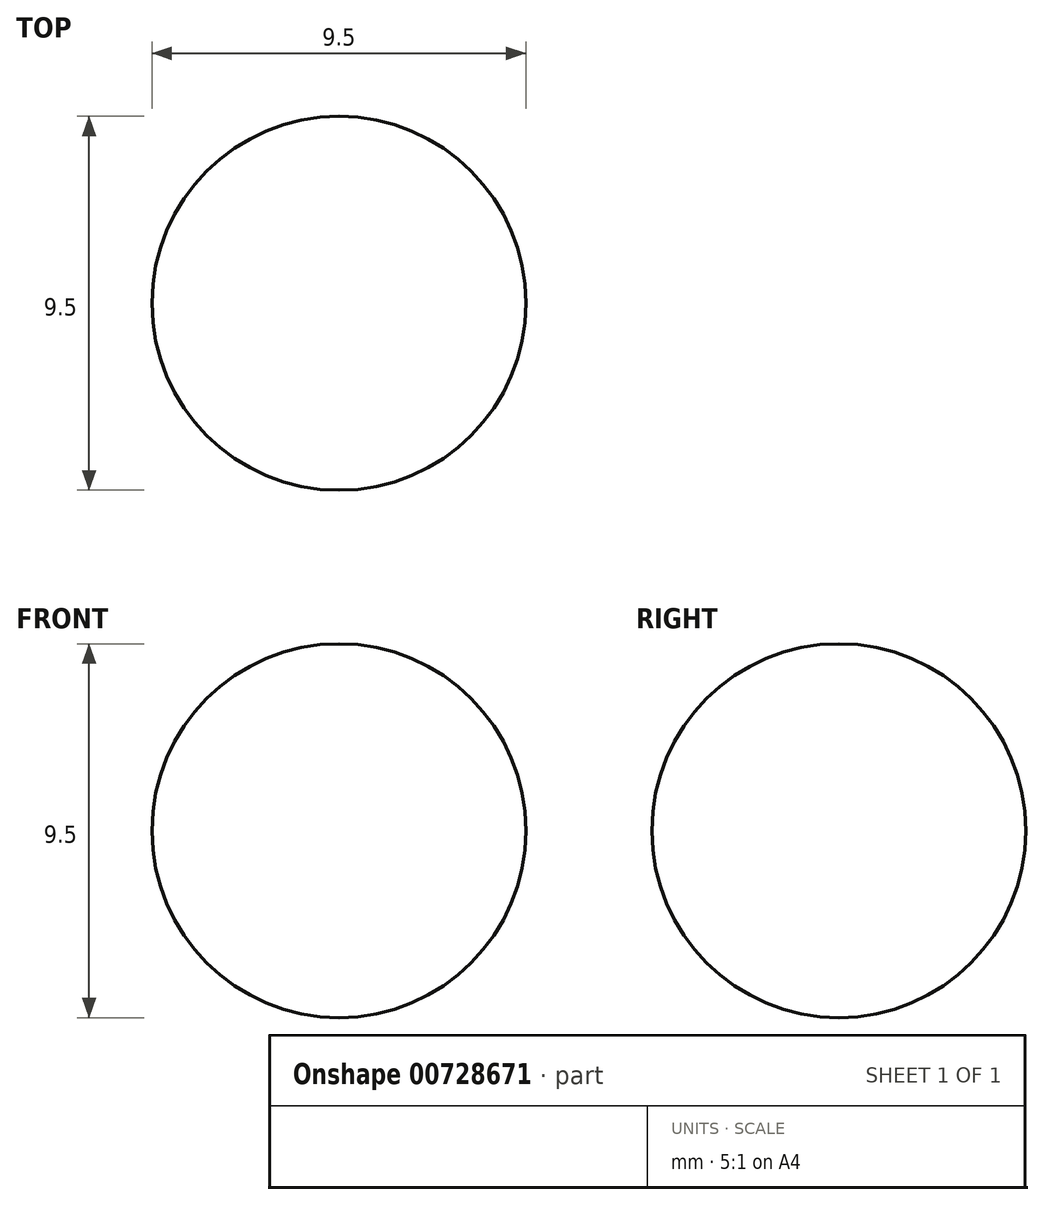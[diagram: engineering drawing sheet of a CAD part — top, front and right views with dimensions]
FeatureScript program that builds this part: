
annotation { "Feature Type Name" : "Feature", "Feature Type Description" : "" }
export const myFeature = defineFeature(function(context is Context, id is Id, definition is map)
    precondition{}
    {
        {
            var Q0;
            Q0=qCreatedBy(makeId("Front.planeOp"),FACE);
            var sketch = newSketch(context, id + "F0", { "sketchPlane" : qUnion([Q0])});
            skCircle(sketch, "E0", {"center": v(0, 0) * mm, "radius": 4.75 * mm});
            skLineSegment(sketch, "E1", {"start": v(-4.75, 0) * mm, "end": v(4.75, 0) * mm});
            skSolve(sketch);
        }
        {
            var Q0;
            {var subQ0=sQuery(id+"F0.wireOp",EDGE,"E1");Q0=makeQuery(id+"F0.imprint","IMPRINT",FACE,{"disambiguationData":[TD([[makeQuery(id+"F0.imprint","IMPRINT",EDGE,{"derivedFrom":subQ0}),1.0]])]});}
            var Q1;
            Q1=sQuery(id+"F0.wireOp",EDGE,"E1");
            revolve(context, id + "F1", {"surfaceOperationType" : NewSurfaceOperationType.NEW, "entities" : qUnion([Q0]), "axis" : qUnion([Q1]), "revolveType" : RevolveType.FULL});
        }
    });
